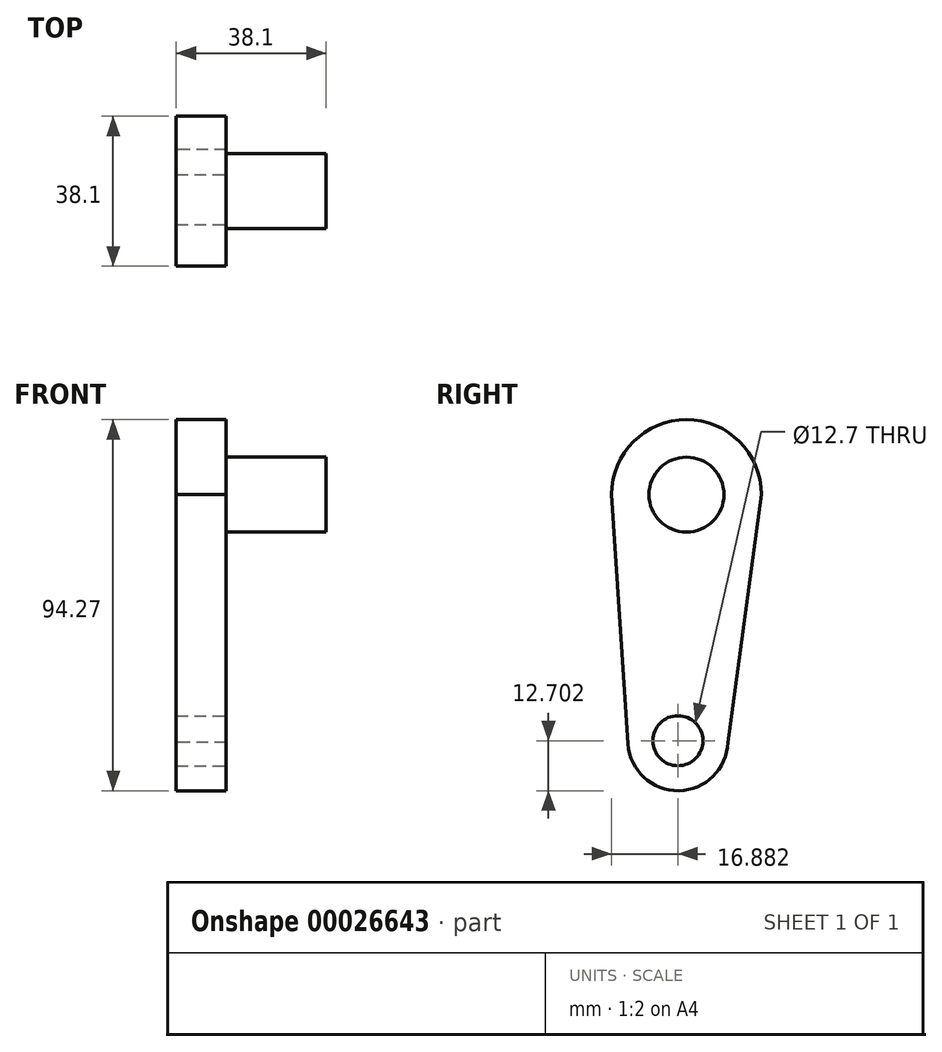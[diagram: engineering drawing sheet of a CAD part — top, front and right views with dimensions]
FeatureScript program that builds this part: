
annotation { "Feature Type Name" : "Feature", "Feature Type Description" : "" }
export const myFeature = defineFeature(function(context is Context, id is Id, definition is map)
    precondition{}
    {
        {
            var Q0;
            Q0=qCreatedBy(makeId("Right.planeOp"),FACE);
            var sketch = newSketch(context, id + "F0", { "sketchPlane" : qUnion([Q0])});
            skArc(sketch, "E0", {"start": v(19.05, 0) * mm, "mid": v(0, 19.05) * mm, "end": v(-19.05, 0) * mm});
            skLineSegment(sketch, "E1", {"start": v(19.05, 0) * mm, "end": v(10.53, -62.93) * mm});
            skLineSegment(sketch, "E2", {"start": v(-19.05, 0) * mm, "end": v(-14.84, -63.36) * mm});
            skArc(sketch, "E3", {"start": v(-14.84, -63.36) * mm, "mid": v(-1.95, -75.22) * mm, "end": v(10.53, -62.93) * mm});
            skCircle(sketch, "E4", {"center": v(0, 0) * mm, "radius": 9.53 * mm});
            skSolve(sketch);
        }
        {
            var Q0;
            Q0=makeQuery(id+"F0.imprint","IMPRINT",FACE,{"disambiguationData":[TD([[makeQuery(id+"F0.imprint","IMPRINT",EDGE,{"derivedFrom":sQuery(id+"F0.wireOp",EDGE,"E4")}),1.0]])]});
            var Q1;
            Q1=makeQuery(id+"F0.imprint","IMPRINT",FACE,{"disambiguationData":[TD([[makeQuery(id+"F0.imprint","IMPRINT",EDGE,{"derivedFrom":sQuery(id+"F0.wireOp",EDGE,"E0")}),1.0]])]});
            extrude(context, id + "F1", {"entities" : qUnion([Q0, Q1]), "depth" : 12.7 * mm});
        }
        {
            var Q0;
            Q0=makeQuery(id+"F0.imprint","IMPRINT",FACE,{"disambiguationData":[TD([[makeQuery(id+"F0.imprint","IMPRINT",EDGE,{"derivedFrom":sQuery(id+"F0.wireOp",EDGE,"E4")}),1.0]])]});
            extrude(context, id + "F2", {"entities" : qUnion([Q0]), "operationType" : NewBodyOperationType.ADD, "depth" : 38.1 * mm});
        }
        {
            var Q0;
            Q0=makeQuery(id+"F1.opExtrude","CAP_FACE",FACE,{"disambiguationData":[OSD([sQuery(id+"F0.wireOp",EDGE,"E0"),sQuery(id+"F0.wireOp",EDGE,"E1"),sQuery(id+"F0.wireOp",EDGE,"E2"),sQuery(id+"F0.wireOp",EDGE,"E3")])],"isStart":false});
            var sketch = newSketch(context, id + "F3", { "sketchPlane" : qUnion([Q0])});
            skCircle(sketch, "E5", {"center": v(-2.17, -62.52) * mm, "radius": 6.35 * mm});
            skSolve(sketch);
        }
        {
            var Q0;
            Q0=makeQuery(id+"F3.imprint","IMPRINT",FACE,{"disambiguationData":[TD([[makeQuery(id+"F3.imprint","IMPRINT",EDGE,{"derivedFrom":sQuery(id+"F3.wireOp",EDGE,"E5")}),1.0]])]});
            var Q1;
            Q1=sQuery(id+"F3.wireOp",EDGE,"E5");
            extrude(context, id + "F4", {"entities" : qUnion([Q0]), "operationType" : NewBodyOperationType.REMOVE, "surfaceEntities" : qUnion([Q1]), "endBound" : BoundingType.THROUGH_ALL, "oppositeDirection" : true, "depth" : 25.4 * mm});
        }
    });
